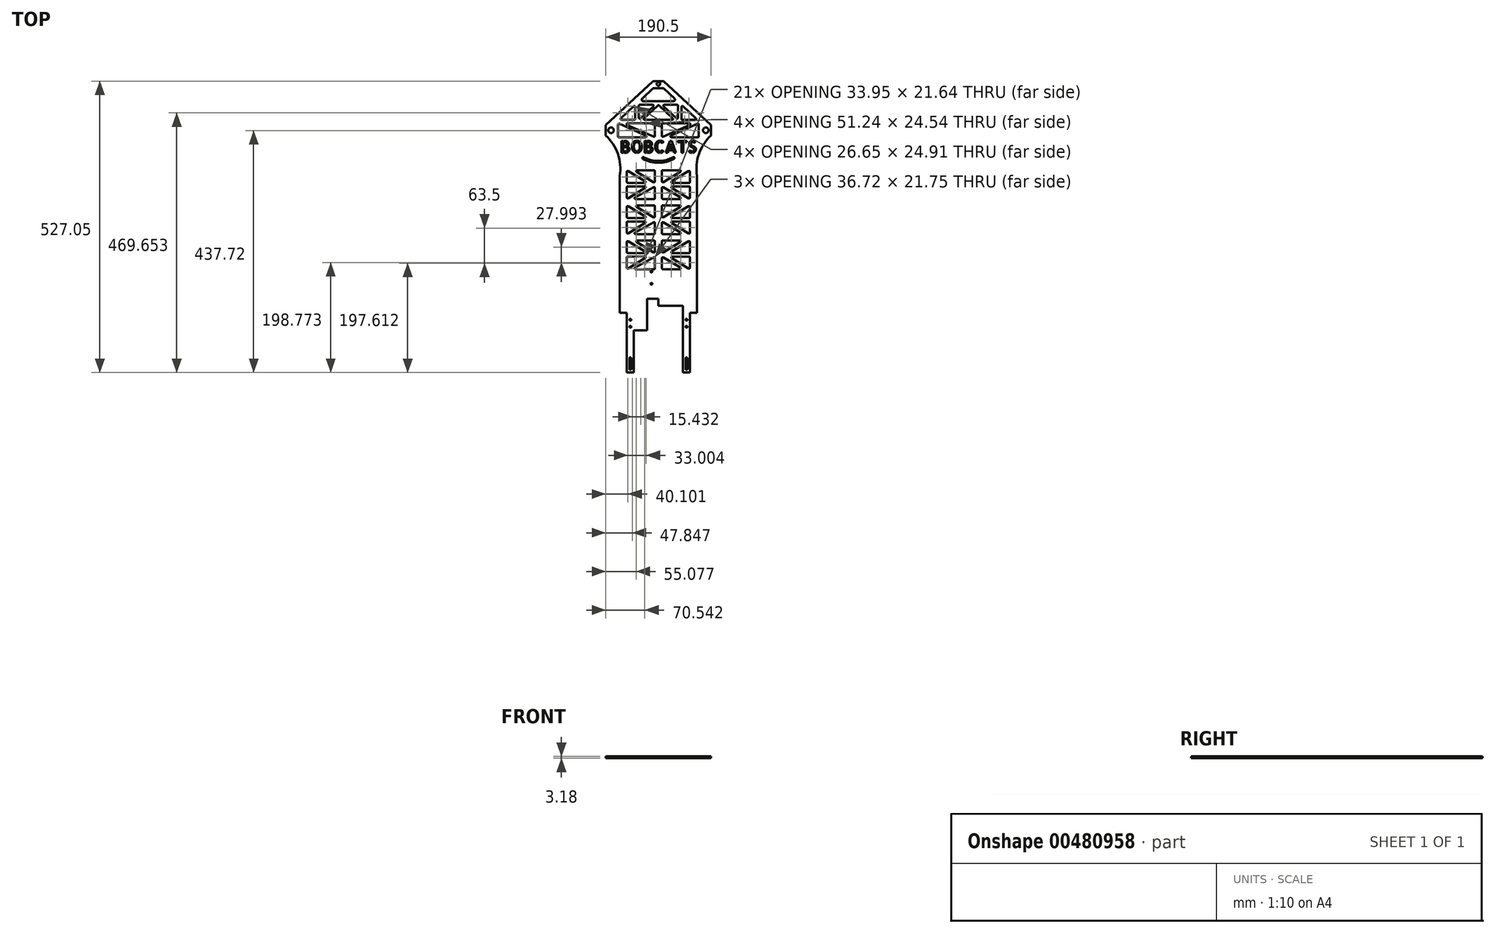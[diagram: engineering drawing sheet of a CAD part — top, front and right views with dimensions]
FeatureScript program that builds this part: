
annotation { "Feature Type Name" : "Feature", "Feature Type Description" : "" }
export const myFeature = defineFeature(function(context is Context, id is Id, definition is map)
    precondition{}
    {
        {
            var Q0;
            Q0=qCreatedBy(makeId("Top.planeOp"),FACE);
            var sketch = newSketch(context, id + "F0", { "sketchPlane" : qUnion([Q0])});
            skLineSegment(sketch, "E0.bottom", {"start": v(0, 0) * mm, "end": v(139.7, 0) * mm});
            skLineSegment(sketch, "E0.left", {"start": v(0, 0) * mm, "end": v(0, 127) * mm});
            skLineSegment(sketch, "E0.right", {"start": v(139.7, 0) * mm, "end": v(139.7, 153) * mm});
            skLineSegment(sketch, "E1.top", {"start": v(12.7, -228.6) * mm, "end": v(25.4, -228.6) * mm});
            skLineSegment(sketch, "E1.left", {"start": v(0, 0) * mm, "end": v(0, -120.65) * mm});
            skLineSegment(sketch, "E1.right", {"start": v(139.7, 0) * mm, "end": v(139.7, -120.65) * mm});
            skPoint(sketch, "E1.middle", {"position": v(69.85, -114.3) * mm});
            skLineSegment(sketch, "E2.top", {"start": v(25.4, -152.4) * mm, "end": v(49.53, -152.4) * mm});
            skLineSegment(sketch, "E2.left", {"start": v(25.4, -228.6) * mm, "end": v(25.4, -152.4) * mm});
            skLineSegment(sketch, "E2.right", {"start": v(114.3, -228.6) * mm, "end": v(114.3, -152.4) * mm});
            skLineSegment(sketch, "E3.top", {"start": v(114.3, -107.95) * mm, "end": v(69.85, -107.95) * mm});
            skLineSegment(sketch, "E3.left", {"start": v(114.3, -152.4) * mm, "end": v(114.3, -107.95) * mm});
            skLineSegment(sketch, "E4.top", {"start": v(69.85, -95.25) * mm, "end": v(49.53, -95.25) * mm});
            skLineSegment(sketch, "E4.left", {"start": v(69.85, -107.95) * mm, "end": v(69.85, -95.25) * mm});
            skLineSegment(sketch, "E4.right", {"start": v(49.53, -152.4) * mm, "end": v(49.53, -95.25) * mm});
            skLineSegment(sketch, "E5.left", {"start": v(25.4, -228.6) * mm, "end": v(25.4, -222.25) * mm});
            skLineSegment(sketch, "E5.right", {"start": v(114.3, -107.11) * mm, "end": v(114.3, -100.76) * mm});
            skPoint(sketch, "E6", {"position": v(57.15, -46.04) * mm});
            skPoint(sketch, "E7", {"position": v(57.15, -68.26) * mm});
            skCircle(sketch, "E8", {"center": v(57.15, -68.26) * mm, "radius": 1.59 * mm});
            skCircle(sketch, "E9", {"center": v(57.15, -46.04) * mm, "radius": 1.59 * mm});
            skLineSegment(sketch, "E10.top", {"start": v(0, -120.65) * mm, "end": v(12.7, -120.65) * mm});
            skLineSegment(sketch, "E10.right", {"start": v(12.7, -228.6) * mm, "end": v(12.7, -120.65) * mm});
            skPoint(sketch, "E11.oppositeSnap0", {"position": v(59.7, -152.4) * mm});
            skLineSegment(sketch, "E12.top", {"start": v(127, -120.65) * mm, "end": v(139.7, -120.65) * mm});
            skLineSegment(sketch, "E12.left", {"start": v(127, -228.6) * mm, "end": v(127, -120.65) * mm});
            skPoint(sketch, "E13.orphan", {"position": v(0, -228.6) * mm});
            skPoint(sketch, "E14.orphan", {"position": v(139.7, -228.6) * mm});
            skLineSegment(sketch, "E15.trimOffspring", {"start": v(114.3, -228.6) * mm, "end": v(127, -228.6) * mm});
            skPoint(sketch, "E3.bottom.end.orphan", {"position": v(69.85, -152.4) * mm});
            skLineSegment(sketch, "E16.bottom", {"start": v(60.32, 298.45) * mm, "end": v(79.38, 298.45) * mm});
            skLineSegment(sketch, "E16.top", {"start": v(0, 127) * mm, "end": v(139.7, 127) * mm});
            skLineSegment(sketch, "E16.left", {"start": v(-25.4, 219.08) * mm, "end": v(-25.4, 200.02) * mm});
            skLineSegment(sketch, "E16.right", {"start": v(165.1, 219.08) * mm, "end": v(165.1, 200.02) * mm});
            skLineSegment(sketch, "E17", {"start": v(60.32, 298.45) * mm, "end": v(-25.4, 219.08) * mm});
            skLineSegment(sketch, "E18", {"start": v(79.38, 298.45) * mm, "end": v(165.1, 219.08) * mm});
            skPoint(sketch, "E19", {"position": v(69.85, 293.37) * mm});
            skPoint(sketch, "E19.positionSnap0", {"position": v(69.85, 298.45) * mm});
            skCircle(sketch, "E20", {"center": v(69.85, 293.37) * mm, "radius": 3.2 * mm});
            skLineSegment(sketch, "E21.bottom", {"start": v(64.34, 298.45) * mm, "end": v(74.5, 298.45) * mm});
            skPoint(sketch, "E22", {"position": v(69.85, 127) * mm});
            skPoint(sketch, "E23", {"position": v(-25.4, 209.55) * mm});
            skPoint(sketch, "E24", {"position": v(165.1, 209.55) * mm});
            skText(sketch, "E25", { "text": "BOBCATS", "fontName": "AllertaStencil-Regular.ttf"});
            skArc(sketch, "E26", {"start": v(0, 127) * mm, "mid": v(-3.47, 166.72) * mm, "end": v(-25.4, 200.03) * mm});
            skLineSegment(sketch, "E27", {"start": v(42.39, 159.43) * mm, "end": v(100.33, 159.43) * mm, "construction": true});
            skArc(sketch, "E28", {"start": v(42.39, 159.43) * mm, "mid": v(69.85, 152.4) * mm, "end": v(97.31, 159.43) * mm, "construction": true});
            skArc(sketch, "E29.0", {"start": v(43.16, 160.83) * mm, "mid": v(69.85, 154) * mm, "end": v(96.54, 160.83) * mm});
            skArc(sketch, "E30.0", {"start": v(41.62, 158.03) * mm, "mid": v(69.85, 150.8) * mm, "end": v(98.08, 158.03) * mm});
            skCircle(sketch, "E31", {"center": v(42.39, 159.43) * mm, "radius": 1.6 * mm});
            skCircle(sketch, "E32", {"center": v(97.31, 159.43) * mm, "radius": 1.6 * mm});
            skLineSegment(sketch, "E33", {"start": v(59.72, 284.9) * mm, "end": v(40.83, 267.42) * mm});
            skLineSegment(sketch, "E34", {"start": v(42.99, 261.91) * mm, "end": v(96.71, 261.91) * mm});
            skLineSegment(sketch, "E35", {"start": v(98.87, 267.42) * mm, "end": v(79.98, 284.9) * mm});
            skLineSegment(sketch, "E36", {"start": v(77.83, 285.75) * mm, "end": v(61.87, 285.75) * mm});
            skPoint(sketch, "E37.visualSharp", {"position": v(60.63, 285.75) * mm});
            skArc(sketch, "E37.filletArc", {"start": v(61.87, 285.75) * mm, "mid": v(60.71, 285.53) * mm, "end": v(59.72, 284.9) * mm});
            skPoint(sketch, "E38.visualSharp", {"position": v(79.07, 285.75) * mm});
            skArc(sketch, "E38.filletArc", {"start": v(79.98, 284.9) * mm, "mid": v(78.99, 285.53) * mm, "end": v(77.83, 285.75) * mm});
            skPoint(sketch, "E39.visualSharp", {"position": v(34.89, 261.91) * mm});
            skArc(sketch, "E39.filletArc", {"start": v(40.83, 267.42) * mm, "mid": v(40.03, 263.93) * mm, "end": v(42.99, 261.91) * mm});
            skPoint(sketch, "E40.visualSharp", {"position": v(104.81, 261.91) * mm});
            skArc(sketch, "E40.filletArc", {"start": v(96.71, 261.91) * mm, "mid": v(99.67, 263.93) * mm, "end": v(98.87, 267.42) * mm});
            skCircle(sketch, "E41", {"center": v(-15.88, 209.55) * mm, "radius": 5 * mm});
            skCircle(sketch, "E42", {"center": v(155.58, 209.55) * mm, "radius": 5 * mm});
            skLineSegment(sketch, "E43", {"start": v(-3.18, 198.44) * mm, "end": v(-3.18, 219.8) * mm});
            skLineSegment(sketch, "E44", {"start": v(-0.94, 221.26) * mm, "end": v(47.14, 199.89) * mm});
            skLineSegment(sketch, "E45", {"start": v(46.5, 196.85) * mm, "end": v(-1.59, 196.85) * mm});
            skLineSegment(sketch, "E46", {"start": v(13.19, 219.21) * mm, "end": v(61.27, 197.84) * mm});
            skLineSegment(sketch, "E47", {"start": v(63.5, 199.3) * mm, "end": v(63.5, 220.66) * mm});
            skLineSegment(sketch, "E48", {"start": v(61.91, 222.25) * mm, "end": v(13.83, 222.25) * mm});
            skLineSegment(sketch, "E49", {"start": v(142.88, 198.44) * mm, "end": v(142.88, 219.8) * mm});
            skLineSegment(sketch, "E50", {"start": v(140.64, 221.26) * mm, "end": v(92.56, 199.89) * mm});
            skLineSegment(sketch, "E51", {"start": v(93.2, 196.85) * mm, "end": v(141.29, 196.85) * mm});
            skLineSegment(sketch, "E52", {"start": v(76.2, 199.3) * mm, "end": v(76.2, 220.66) * mm});
            skLineSegment(sketch, "E53", {"start": v(78.43, 197.84) * mm, "end": v(126.51, 219.21) * mm});
            skLineSegment(sketch, "E54", {"start": v(125.87, 222.25) * mm, "end": v(77.79, 222.25) * mm});
            skPoint(sketch, "E55.visualSharp", {"position": v(6.35, 222.25) * mm});
            skArc(sketch, "E55.filletArc", {"start": v(13.83, 222.25) * mm, "mid": v(12.28, 221) * mm, "end": v(13.19, 219.21) * mm});
            skPoint(sketch, "E56.visualSharp", {"position": v(53.98, 196.85) * mm});
            skArc(sketch, "E56.filletArc", {"start": v(46.5, 196.85) * mm, "mid": v(48.05, 198.1) * mm, "end": v(47.14, 199.89) * mm});
            skPoint(sketch, "E57.visualSharp", {"position": v(-3.18, 222.25) * mm});
            skArc(sketch, "E57.filletArc", {"start": v(-0.94, 221.26) * mm, "mid": v(-2.45, 221.14) * mm, "end": v(-3.18, 219.8) * mm});
            skPoint(sketch, "E58.visualSharp", {"position": v(-3.18, 196.85) * mm});
            skArc(sketch, "E58.filletArc", {"start": v(-3.18, 198.44) * mm, "mid": v(-2.71, 197.31) * mm, "end": v(-1.59, 196.85) * mm});
            skPoint(sketch, "E59.visualSharp", {"position": v(76.2, 222.25) * mm});
            skArc(sketch, "E59.filletArc", {"start": v(77.79, 222.25) * mm, "mid": v(76.66, 221.79) * mm, "end": v(76.2, 220.66) * mm});
            skPoint(sketch, "E60.visualSharp", {"position": v(63.5, 222.25) * mm});
            skArc(sketch, "E60.filletArc", {"start": v(63.5, 220.66) * mm, "mid": v(63.04, 221.79) * mm, "end": v(61.91, 222.25) * mm});
            skPoint(sketch, "E61.visualSharp", {"position": v(63.5, 196.85) * mm});
            skArc(sketch, "E61.filletArc", {"start": v(61.27, 197.84) * mm, "mid": v(62.78, 197.96) * mm, "end": v(63.5, 199.3) * mm});
            skPoint(sketch, "E62.visualSharp", {"position": v(76.2, 196.85) * mm});
            skArc(sketch, "E62.filletArc", {"start": v(76.2, 199.3) * mm, "mid": v(76.92, 197.96) * mm, "end": v(78.43, 197.84) * mm});
            skPoint(sketch, "E63.visualSharp", {"position": v(133.35, 222.25) * mm});
            skArc(sketch, "E63.filletArc", {"start": v(126.51, 219.21) * mm, "mid": v(127.42, 221) * mm, "end": v(125.87, 222.25) * mm});
            skPoint(sketch, "E64.visualSharp", {"position": v(85.72, 196.85) * mm});
            skArc(sketch, "E64.filletArc", {"start": v(92.56, 199.89) * mm, "mid": v(91.65, 198.1) * mm, "end": v(93.2, 196.85) * mm});
            skPoint(sketch, "E65.visualSharp", {"position": v(142.88, 222.25) * mm});
            skArc(sketch, "E65.filletArc", {"start": v(142.88, 219.8) * mm, "mid": v(142.15, 221.14) * mm, "end": v(140.64, 221.26) * mm});
            skPoint(sketch, "E66.visualSharp", {"position": v(142.88, 196.85) * mm});
            skArc(sketch, "E66.filletArc", {"start": v(141.29, 196.85) * mm, "mid": v(142.41, 197.31) * mm, "end": v(142.88, 198.44) * mm});
            skLineSegment(sketch, "E67", {"start": v(68.77, 254.57) * mm, "end": v(43.7, 231.35) * mm});
            skLineSegment(sketch, "E68", {"start": v(44.78, 228.6) * mm, "end": v(94.92, 228.6) * mm});
            skLineSegment(sketch, "E69", {"start": v(96, 231.35) * mm, "end": v(70.93, 254.57) * mm});
            skLineSegment(sketch, "E70", {"start": v(60.53, 252.81) * mm, "end": v(37.04, 231.07) * mm});
            skLineSegment(sketch, "E71", {"start": v(34.38, 232.23) * mm, "end": v(34.38, 253.98) * mm});
            skLineSegment(sketch, "E72", {"start": v(35.97, 255.56) * mm, "end": v(59.45, 255.56) * mm});
            skLineSegment(sketch, "E73", {"start": v(25.36, 253.1) * mm, "end": v(1.88, 231.35) * mm});
            skLineSegment(sketch, "E74", {"start": v(2.96, 228.6) * mm, "end": v(26.44, 228.6) * mm});
            skLineSegment(sketch, "E75", {"start": v(28.03, 230.19) * mm, "end": v(28.03, 251.93) * mm});
            skPoint(sketch, "E76.visualSharp", {"position": v(28.03, 255.56) * mm});
            skArc(sketch, "E76.filletArc", {"start": v(28.03, 251.93) * mm, "mid": v(27.08, 253.39) * mm, "end": v(25.36, 253.1) * mm});
            skPoint(sketch, "E77.visualSharp", {"position": v(-1.1, 228.6) * mm});
            skArc(sketch, "E77.filletArc", {"start": v(1.88, 231.35) * mm, "mid": v(1.48, 229.6) * mm, "end": v(2.96, 228.6) * mm});
            skPoint(sketch, "E78.visualSharp", {"position": v(28.03, 228.6) * mm});
            skArc(sketch, "E78.filletArc", {"start": v(26.44, 228.6) * mm, "mid": v(27.56, 229.06) * mm, "end": v(28.03, 230.19) * mm});
            skPoint(sketch, "E79.visualSharp", {"position": v(34.38, 228.6) * mm});
            skArc(sketch, "E79.filletArc", {"start": v(34.38, 232.23) * mm, "mid": v(35.33, 230.78) * mm, "end": v(37.04, 231.07) * mm});
            skPoint(sketch, "E80.visualSharp", {"position": v(34.38, 255.56) * mm});
            skArc(sketch, "E80.filletArc", {"start": v(35.97, 255.56) * mm, "mid": v(34.84, 255.1) * mm, "end": v(34.38, 253.98) * mm});
            skPoint(sketch, "E81.visualSharp", {"position": v(63.5, 255.56) * mm});
            skArc(sketch, "E81.filletArc", {"start": v(60.53, 252.81) * mm, "mid": v(60.93, 254.56) * mm, "end": v(59.45, 255.56) * mm});
            skPoint(sketch, "E82.visualSharp", {"position": v(69.85, 255.56) * mm});
            skArc(sketch, "E82.filletArc", {"start": v(70.93, 254.57) * mm, "mid": v(69.85, 254.99) * mm, "end": v(68.77, 254.57) * mm});
            skPoint(sketch, "E83.visualSharp", {"position": v(40.73, 228.6) * mm});
            skArc(sketch, "E83.filletArc", {"start": v(43.7, 231.35) * mm, "mid": v(43.3, 229.6) * mm, "end": v(44.78, 228.6) * mm});
            skPoint(sketch, "E84.visualSharp", {"position": v(98.97, 228.6) * mm});
            skArc(sketch, "E84.filletArc", {"start": v(94.92, 228.6) * mm, "mid": v(96.4, 229.6) * mm, "end": v(96, 231.35) * mm});
            skLineSegment(sketch, "E85", {"start": v(69.85, 260.44) * mm, "end": v(69.85, 219.43) * mm});
            skLineSegment(sketch, "E86.MirrorCS", {"start": v(79.17, 252.81) * mm, "end": v(102.66, 231.07) * mm});
            skLineSegment(sketch, "E87.MirrorCS", {"start": v(103.73, 255.56) * mm, "end": v(80.25, 255.56) * mm});
            skLineSegment(sketch, "E88.MirrorCS", {"start": v(105.32, 232.23) * mm, "end": v(105.32, 253.98) * mm});
            skLineSegment(sketch, "E89.MirrorCS", {"start": v(111.67, 230.19) * mm, "end": v(111.67, 251.93) * mm});
            skLineSegment(sketch, "E90.MirrorCS", {"start": v(114.34, 253.1) * mm, "end": v(137.82, 231.35) * mm});
            skLineSegment(sketch, "E91.MirrorCS", {"start": v(136.74, 228.6) * mm, "end": v(113.26, 228.6) * mm});
            skArc(sketch, "E92.MirrorCS", {"start": v(111.67, 251.93) * mm, "mid": v(112.62, 253.39) * mm, "end": v(114.34, 253.1) * mm});
            skArc(sketch, "E93.MirrorCS", {"start": v(113.26, 228.6) * mm, "mid": v(112.14, 229.06) * mm, "end": v(111.67, 230.19) * mm});
            skArc(sketch, "E94.MirrorCS", {"start": v(105.32, 232.23) * mm, "mid": v(104.37, 230.78) * mm, "end": v(102.66, 231.07) * mm});
            skArc(sketch, "E95.MirrorCS", {"start": v(103.73, 255.56) * mm, "mid": v(104.86, 255.1) * mm, "end": v(105.32, 253.98) * mm});
            skArc(sketch, "E96.MirrorCS", {"start": v(79.17, 252.81) * mm, "mid": v(78.77, 254.56) * mm, "end": v(80.25, 255.56) * mm});
            skArc(sketch, "E97.MirrorCS", {"start": v(137.82, 231.35) * mm, "mid": v(138.22, 229.6) * mm, "end": v(136.74, 228.6) * mm});
            skLineSegment(sketch, "E98", {"start": v(12.7, 115.93) * mm, "end": v(12.7, 134.4) * mm});
            skLineSegment(sketch, "E99", {"start": v(15.1, 135.76) * mm, "end": v(45.89, 117.3) * mm});
            skLineSegment(sketch, "E100", {"start": v(45.07, 114.35) * mm, "end": v(14.29, 114.35) * mm});
            skLineSegment(sketch, "E101", {"start": v(30.31, 134.26) * mm, "end": v(61.1, 115.79) * mm});
            skLineSegment(sketch, "E102", {"start": v(63.5, 117.15) * mm, "end": v(63.5, 135.62) * mm});
            skLineSegment(sketch, "E103", {"start": v(61.91, 137.2) * mm, "end": v(31.13, 137.2) * mm});
            skLineSegment(sketch, "E104", {"start": v(76.2, 135.62) * mm, "end": v(76.2, 117.15) * mm});
            skLineSegment(sketch, "E105", {"start": v(78.6, 115.79) * mm, "end": v(109.39, 134.26) * mm});
            skLineSegment(sketch, "E106", {"start": v(108.57, 137.2) * mm, "end": v(77.79, 137.2) * mm});
            skLineSegment(sketch, "E107", {"start": v(124.6, 135.76) * mm, "end": v(93.81, 117.3) * mm});
            skLineSegment(sketch, "E108", {"start": v(94.63, 114.35) * mm, "end": v(125.41, 114.35) * mm});
            skLineSegment(sketch, "E109", {"start": v(127, 115.93) * mm, "end": v(127, 134.4) * mm});
            skArc(sketch, "E110.MirrorCS", {"start": v(139.7, 127) * mm, "mid": v(143.17, 166.72) * mm, "end": v(165.1, 200.03) * mm});
            skLineSegment(sketch, "E111", {"start": v(14.29, 108) * mm, "end": v(45.07, 108) * mm});
            skLineSegment(sketch, "E112", {"start": v(45.89, 105.05) * mm, "end": v(15.1, 86.58) * mm});
            skLineSegment(sketch, "E113", {"start": v(12.7, 87.94) * mm, "end": v(12.7, 106.4) * mm});
            skLineSegment(sketch, "E114", {"start": v(63.5, 105.3) * mm, "end": v(63.5, 86.72) * mm});
            skLineSegment(sketch, "E115", {"start": v(61.91, 85.14) * mm, "end": v(28.37, 85.14) * mm});
            skLineSegment(sketch, "E116", {"start": v(27.6, 88.11) * mm, "end": v(61.14, 106.69) * mm});
            skLineSegment(sketch, "E117", {"start": v(76.2, 105.2) * mm, "end": v(76.2, 86.72) * mm});
            skLineSegment(sketch, "E118", {"start": v(77.79, 85.14) * mm, "end": v(108.57, 85.14) * mm});
            skLineSegment(sketch, "E119", {"start": v(109.39, 88.08) * mm, "end": v(78.6, 106.55) * mm});
            skLineSegment(sketch, "E120", {"start": v(93.81, 105.05) * mm, "end": v(124.6, 86.58) * mm});
            skLineSegment(sketch, "E121", {"start": v(127, 87.94) * mm, "end": v(127, 106.4) * mm});
            skLineSegment(sketch, "E122", {"start": v(125.41, 108) * mm, "end": v(94.63, 108) * mm});
            skPoint(sketch, "E123.visualSharp", {"position": v(12.7, 114.35) * mm});
            skArc(sketch, "E123.filletArc", {"start": v(12.7, 115.93) * mm, "mid": v(13.16, 114.81) * mm, "end": v(14.29, 114.35) * mm});
            skPoint(sketch, "E124.visualSharp", {"position": v(50.8, 114.35) * mm});
            skArc(sketch, "E124.filletArc", {"start": v(45.07, 114.35) * mm, "mid": v(46.6, 115.5) * mm, "end": v(45.89, 117.3) * mm});
            skPoint(sketch, "E125.visualSharp", {"position": v(12.7, 137.2) * mm});
            skArc(sketch, "E125.filletArc", {"start": v(15.1, 135.76) * mm, "mid": v(13.5, 135.78) * mm, "end": v(12.7, 134.4) * mm});
            skPoint(sketch, "E126.visualSharp", {"position": v(25.4, 137.2) * mm});
            skArc(sketch, "E126.filletArc", {"start": v(31.13, 137.2) * mm, "mid": v(29.6, 136.04) * mm, "end": v(30.31, 134.26) * mm});
            skPoint(sketch, "E127.visualSharp", {"position": v(63.5, 137.2) * mm});
            skArc(sketch, "E127.filletArc", {"start": v(63.5, 135.62) * mm, "mid": v(63.04, 136.74) * mm, "end": v(61.91, 137.2) * mm});
            skPoint(sketch, "E128.visualSharp", {"position": v(63.5, 114.35) * mm});
            skArc(sketch, "E128.filletArc", {"start": v(61.1, 115.79) * mm, "mid": v(62.7, 115.77) * mm, "end": v(63.5, 117.15) * mm});
            skPoint(sketch, "E129.visualSharp", {"position": v(76.2, 114.35) * mm});
            skArc(sketch, "E129.filletArc", {"start": v(76.2, 117.15) * mm, "mid": v(77, 115.77) * mm, "end": v(78.6, 115.79) * mm});
            skPoint(sketch, "E130.visualSharp", {"position": v(114.3, 137.2) * mm});
            skArc(sketch, "E130.filletArc", {"start": v(109.39, 134.26) * mm, "mid": v(110.1, 136.04) * mm, "end": v(108.57, 137.2) * mm});
            skPoint(sketch, "E131.visualSharp", {"position": v(76.2, 137.2) * mm});
            skArc(sketch, "E131.filletArc", {"start": v(77.79, 137.2) * mm, "mid": v(76.66, 136.74) * mm, "end": v(76.2, 135.62) * mm});
            skPoint(sketch, "E132.visualSharp", {"position": v(127, 137.2) * mm});
            skArc(sketch, "E132.filletArc", {"start": v(127, 134.4) * mm, "mid": v(126.2, 135.78) * mm, "end": v(124.6, 135.76) * mm});
            skPoint(sketch, "E133.visualSharp", {"position": v(88.9, 114.35) * mm});
            skArc(sketch, "E133.filletArc", {"start": v(93.81, 117.3) * mm, "mid": v(93.1, 115.5) * mm, "end": v(94.63, 114.35) * mm});
            skPoint(sketch, "E134.visualSharp", {"position": v(127, 114.35) * mm});
            skArc(sketch, "E134.filletArc", {"start": v(125.41, 114.35) * mm, "mid": v(126.54, 114.81) * mm, "end": v(127, 115.93) * mm});
            skPoint(sketch, "E135.visualSharp", {"position": v(12.7, 108) * mm});
            skArc(sketch, "E135.filletArc", {"start": v(14.29, 108) * mm, "mid": v(13.16, 107.53) * mm, "end": v(12.7, 106.4) * mm});
            skPoint(sketch, "E136.visualSharp", {"position": v(50.8, 108) * mm});
            skArc(sketch, "E136.filletArc", {"start": v(45.89, 105.05) * mm, "mid": v(46.6, 106.83) * mm, "end": v(45.07, 108) * mm});
            skPoint(sketch, "E137.visualSharp", {"position": v(63.5, 108) * mm});
            skArc(sketch, "E137.filletArc", {"start": v(63.5, 105.3) * mm, "mid": v(62.72, 106.67) * mm, "end": v(61.14, 106.69) * mm});
            skPoint(sketch, "E138.visualSharp", {"position": v(63.5, 85.14) * mm});
            skArc(sketch, "E138.filletArc", {"start": v(61.91, 85.14) * mm, "mid": v(63.04, 85.6) * mm, "end": v(63.5, 86.72) * mm});
            skPoint(sketch, "E139.visualSharp", {"position": v(22.23, 85.14) * mm});
            skArc(sketch, "E139.filletArc", {"start": v(27.6, 88.11) * mm, "mid": v(26.83, 86.33) * mm, "end": v(28.37, 85.14) * mm});
            skPoint(sketch, "E140.visualSharp", {"position": v(76.2, 85.14) * mm});
            skArc(sketch, "E140.filletArc", {"start": v(76.2, 86.72) * mm, "mid": v(76.66, 85.6) * mm, "end": v(77.79, 85.14) * mm});
            skPoint(sketch, "E141.visualSharp", {"position": v(114.3, 85.14) * mm});
            skArc(sketch, "E141.filletArc", {"start": v(108.57, 85.14) * mm, "mid": v(110.1, 86.3) * mm, "end": v(109.39, 88.08) * mm});
            skPoint(sketch, "E142.visualSharp", {"position": v(76.2, 108) * mm});
            skArc(sketch, "E142.filletArc", {"start": v(78.6, 106.55) * mm, "mid": v(77, 106.57) * mm, "end": v(76.2, 105.2) * mm});
            skPoint(sketch, "E143.visualSharp", {"position": v(88.9, 108) * mm});
            skArc(sketch, "E143.filletArc", {"start": v(94.63, 108) * mm, "mid": v(93.1, 106.83) * mm, "end": v(93.81, 105.05) * mm});
            skPoint(sketch, "E144.visualSharp", {"position": v(127, 108) * mm});
            skArc(sketch, "E144.filletArc", {"start": v(127, 106.4) * mm, "mid": v(126.54, 107.53) * mm, "end": v(125.41, 108) * mm});
            skPoint(sketch, "E145.visualSharp", {"position": v(127, 85.14) * mm});
            skArc(sketch, "E145.filletArc", {"start": v(124.6, 86.58) * mm, "mid": v(126.2, 86.56) * mm, "end": v(127, 87.94) * mm});
            skPoint(sketch, "E146.visualSharp", {"position": v(12.7, 85.14) * mm});
            skArc(sketch, "E146.filletArc", {"start": v(12.7, 87.94) * mm, "mid": v(13.5, 86.56) * mm, "end": v(15.1, 86.58) * mm});
            skLineSegment(sketch, "E147.0.1.0", {"start": v(127, 24.44) * mm, "end": v(127, 42.9) * mm});
            skArc(sketch, "E147.0.1.1", {"start": v(108.57, 21.64) * mm, "mid": v(110.1, 22.8) * mm, "end": v(109.39, 24.58) * mm});
            skPoint(sketch, "E147.0.1.2", {"position": v(88.9, 44.5) * mm});
            skLineSegment(sketch, "E147.0.1.3", {"start": v(127, 52.43) * mm, "end": v(127, 70.9) * mm});
            skLineSegment(sketch, "E147.0.1.4", {"start": v(45.07, 50.85) * mm, "end": v(14.29, 50.85) * mm});
            skLineSegment(sketch, "E147.0.1.5", {"start": v(61.91, 73.7) * mm, "end": v(31.13, 73.7) * mm});
            skArc(sketch, "E147.0.1.6", {"start": v(94.63, 44.5) * mm, "mid": v(93.1, 43.33) * mm, "end": v(93.81, 41.55) * mm});
            skLineSegment(sketch, "E147.0.1.7", {"start": v(77.79, 21.64) * mm, "end": v(108.57, 21.64) * mm});
            skPoint(sketch, "E147.0.1.8", {"position": v(127, 44.5) * mm});
            skPoint(sketch, "E147.0.1.9", {"position": v(76.2, 73.7) * mm});
            skPoint(sketch, "E147.0.1.10", {"position": v(127, 21.64) * mm});
            skPoint(sketch, "E147.0.1.11", {"position": v(63.5, 44.5) * mm});
            skArc(sketch, "E147.0.1.12", {"start": v(45.07, 50.85) * mm, "mid": v(46.6, 52) * mm, "end": v(45.89, 53.8) * mm});
            skLineSegment(sketch, "E147.0.1.13", {"start": v(124.6, 72.26) * mm, "end": v(93.81, 53.8) * mm});
            skPoint(sketch, "E147.0.1.14", {"position": v(22.23, 21.64) * mm});
            skPoint(sketch, "E147.0.1.15", {"position": v(63.5, 50.85) * mm});
            skArc(sketch, "E147.0.1.16", {"start": v(61.1, 52.29) * mm, "mid": v(62.7, 52.27) * mm, "end": v(63.5, 53.65) * mm});
            skPoint(sketch, "E147.0.1.17", {"position": v(25.4, 73.7) * mm});
            skPoint(sketch, "E147.0.1.18", {"position": v(63.5, 21.64) * mm});
            skLineSegment(sketch, "E147.0.1.19", {"start": v(61.91, 21.64) * mm, "end": v(28.37, 21.64) * mm});
            skLineSegment(sketch, "E147.0.1.20", {"start": v(30.31, 70.76) * mm, "end": v(61.1, 52.29) * mm});
            skLineSegment(sketch, "E147.0.1.21", {"start": v(63.5, 41.8) * mm, "end": v(63.5, 23.22) * mm});
            skPoint(sketch, "E147.0.1.22", {"position": v(76.2, 50.85) * mm});
            skLineSegment(sketch, "E147.0.1.23", {"start": v(125.41, 44.5) * mm, "end": v(94.63, 44.5) * mm});
            skPoint(sketch, "E147.0.1.24", {"position": v(12.7, 44.5) * mm});
            skArc(sketch, "E147.0.1.25", {"start": v(12.7, 24.44) * mm, "mid": v(13.5, 23.06) * mm, "end": v(15.1, 23.08) * mm});
            skPoint(sketch, "E147.0.1.26", {"position": v(69.85, 63.5) * mm});
            skLineSegment(sketch, "E147.0.1.27", {"start": v(27.6, 24.61) * mm, "end": v(61.14, 43.19) * mm});
            skLineSegment(sketch, "E147.0.1.28", {"start": v(63.5, 53.65) * mm, "end": v(63.5, 72.12) * mm});
            skPoint(sketch, "E147.0.1.29", {"position": v(12.7, 21.64) * mm});
            skPoint(sketch, "E147.0.1.30", {"position": v(76.2, 44.5) * mm});
            skArc(sketch, "E147.0.1.31", {"start": v(15.1, 72.26) * mm, "mid": v(13.5, 72.28) * mm, "end": v(12.7, 70.9) * mm});
            skPoint(sketch, "E147.0.1.32", {"position": v(127, 73.7) * mm});
            skArc(sketch, "E147.0.1.33", {"start": v(63.5, 41.8) * mm, "mid": v(62.72, 43.17) * mm, "end": v(61.14, 43.19) * mm});
            skLineSegment(sketch, "E147.0.1.34", {"start": v(14.29, 44.5) * mm, "end": v(45.07, 44.5) * mm});
            skLineSegment(sketch, "E147.0.1.35", {"start": v(108.57, 73.7) * mm, "end": v(77.79, 73.7) * mm});
            skPoint(sketch, "E147.0.1.36", {"position": v(114.3, 21.64) * mm});
            skLineSegment(sketch, "E147.0.1.37", {"start": v(45.89, 41.55) * mm, "end": v(15.1, 23.08) * mm});
            skPoint(sketch, "E147.0.1.38", {"position": v(63.5, 73.7) * mm});
            skPoint(sketch, "E147.0.1.39", {"position": v(76.2, 21.64) * mm});
            skArc(sketch, "E147.0.1.40", {"start": v(124.6, 23.08) * mm, "mid": v(126.2, 23.06) * mm, "end": v(127, 24.44) * mm});
            skPoint(sketch, "E147.0.1.41", {"position": v(12.7, 73.7) * mm});
            skPoint(sketch, "E147.0.1.42", {"position": v(50.8, 50.85) * mm});
            skLineSegment(sketch, "E147.0.1.43", {"start": v(94.63, 50.85) * mm, "end": v(125.41, 50.85) * mm});
            skPoint(sketch, "E147.0.1.44", {"position": v(88.9, 50.85) * mm});
            skLineSegment(sketch, "E147.0.1.45", {"start": v(12.7, 52.43) * mm, "end": v(12.7, 70.9) * mm});
            skPoint(sketch, "E147.0.1.46", {"position": v(114.3, 73.7) * mm});
            skPoint(sketch, "E147.0.1.47", {"position": v(50.8, 44.5) * mm});
            skLineSegment(sketch, "E147.0.1.48", {"start": v(109.39, 24.58) * mm, "end": v(78.6, 43.05) * mm});
            skArc(sketch, "E147.0.1.49", {"start": v(78.6, 43.05) * mm, "mid": v(77, 43.07) * mm, "end": v(76.2, 41.7) * mm});
            skPoint(sketch, "E147.0.1.50", {"position": v(127, 50.85) * mm});
            skArc(sketch, "E147.0.1.51", {"start": v(127, 70.9) * mm, "mid": v(126.2, 72.28) * mm, "end": v(124.6, 72.26) * mm});
            skLineSegment(sketch, "E147.0.1.52", {"start": v(93.81, 41.55) * mm, "end": v(124.6, 23.08) * mm});
            skLineSegment(sketch, "E147.0.1.53", {"start": v(78.6, 52.29) * mm, "end": v(109.39, 70.76) * mm});
            skArc(sketch, "E147.0.1.54", {"start": v(45.89, 41.55) * mm, "mid": v(46.6, 43.33) * mm, "end": v(45.07, 44.5) * mm});
            skLineSegment(sketch, "E147.0.1.55", {"start": v(15.1, 72.26) * mm, "end": v(45.89, 53.8) * mm});
            skArc(sketch, "E147.0.1.56", {"start": v(27.6, 24.61) * mm, "mid": v(26.83, 22.83) * mm, "end": v(28.37, 21.64) * mm});
            skArc(sketch, "E147.0.1.57", {"start": v(93.81, 53.8) * mm, "mid": v(93.1, 52) * mm, "end": v(94.63, 50.85) * mm});
            skPoint(sketch, "E147.0.1.58", {"position": v(12.7, 50.85) * mm});
            skLineSegment(sketch, "E147.0.1.59", {"start": v(76.2, 72.12) * mm, "end": v(76.2, 53.65) * mm});
            skLineSegment(sketch, "E147.0.1.60", {"start": v(76.2, 41.7) * mm, "end": v(76.2, 23.22) * mm});
            skLineSegment(sketch, "E147.0.1.61", {"start": v(12.7, 24.44) * mm, "end": v(12.7, 42.9) * mm});
            skArc(sketch, "E147.0.1.62", {"start": v(76.2, 53.65) * mm, "mid": v(77, 52.27) * mm, "end": v(78.6, 52.29) * mm});
            skArc(sketch, "E147.0.1.63", {"start": v(12.7, 52.43) * mm, "mid": v(13.16, 51.31) * mm, "end": v(14.29, 50.85) * mm});
            skArc(sketch, "E147.0.1.64", {"start": v(14.29, 44.5) * mm, "mid": v(13.16, 44.03) * mm, "end": v(12.7, 42.9) * mm});
            skArc(sketch, "E147.0.1.65", {"start": v(127, 42.9) * mm, "mid": v(126.54, 44.03) * mm, "end": v(125.41, 44.5) * mm});
            skArc(sketch, "E147.0.1.66", {"start": v(109.39, 70.76) * mm, "mid": v(110.1, 72.54) * mm, "end": v(108.57, 73.7) * mm});
            skArc(sketch, "E147.0.1.67", {"start": v(61.91, 21.64) * mm, "mid": v(63.04, 22.1) * mm, "end": v(63.5, 23.22) * mm});
            skArc(sketch, "E147.0.1.68", {"start": v(31.13, 73.7) * mm, "mid": v(29.6, 72.54) * mm, "end": v(30.31, 70.76) * mm});
            skArc(sketch, "E147.0.1.69", {"start": v(63.5, 72.12) * mm, "mid": v(63.04, 73.24) * mm, "end": v(61.91, 73.7) * mm});
            skArc(sketch, "E147.0.1.70", {"start": v(77.79, 73.7) * mm, "mid": v(76.66, 73.24) * mm, "end": v(76.2, 72.12) * mm});
            skArc(sketch, "E147.0.1.71", {"start": v(76.2, 23.22) * mm, "mid": v(76.66, 22.1) * mm, "end": v(77.79, 21.64) * mm});
            skArc(sketch, "E147.0.1.72", {"start": v(125.41, 50.85) * mm, "mid": v(126.54, 51.31) * mm, "end": v(127, 52.43) * mm});
            skLineSegment(sketch, "E147.0.2.0", {"start": v(127, -39.06) * mm, "end": v(127, -20.6) * mm});
            skArc(sketch, "E147.0.2.1", {"start": v(108.57, -41.86) * mm, "mid": v(110.1, -40.7) * mm, "end": v(109.39, -38.92) * mm});
            skPoint(sketch, "E147.0.2.2", {"position": v(88.9, -19) * mm});
            skLineSegment(sketch, "E147.0.2.3", {"start": v(127, -11.07) * mm, "end": v(127, 7.4) * mm});
            skLineSegment(sketch, "E147.0.2.4", {"start": v(45.07, -12.65) * mm, "end": v(14.29, -12.65) * mm});
            skLineSegment(sketch, "E147.0.2.5", {"start": v(61.91, 10.2) * mm, "end": v(31.13, 10.2) * mm});
            skArc(sketch, "E147.0.2.6", {"start": v(94.63, -19) * mm, "mid": v(93.1, -20.17) * mm, "end": v(93.81, -21.95) * mm});
            skLineSegment(sketch, "E147.0.2.7", {"start": v(77.79, -41.86) * mm, "end": v(108.57, -41.86) * mm});
            skPoint(sketch, "E147.0.2.8", {"position": v(127, -19) * mm});
            skPoint(sketch, "E147.0.2.9", {"position": v(76.2, 10.2) * mm});
            skPoint(sketch, "E147.0.2.10", {"position": v(127, -41.86) * mm});
            skPoint(sketch, "E147.0.2.11", {"position": v(63.5, -19) * mm});
            skArc(sketch, "E147.0.2.12", {"start": v(45.07, -12.65) * mm, "mid": v(46.6, -11.5) * mm, "end": v(45.89, -9.7) * mm});
            skLineSegment(sketch, "E147.0.2.13", {"start": v(124.6, 8.76) * mm, "end": v(93.81, -9.7) * mm});
            skPoint(sketch, "E147.0.2.14", {"position": v(22.23, -41.86) * mm});
            skPoint(sketch, "E147.0.2.15", {"position": v(63.5, -12.65) * mm});
            skArc(sketch, "E147.0.2.16", {"start": v(61.1, -11.21) * mm, "mid": v(62.7, -11.23) * mm, "end": v(63.5, -9.85) * mm});
            skPoint(sketch, "E147.0.2.17", {"position": v(25.4, 10.2) * mm});
            skPoint(sketch, "E147.0.2.18", {"position": v(63.5, -41.86) * mm});
            skLineSegment(sketch, "E147.0.2.19", {"start": v(61.91, -41.86) * mm, "end": v(28.37, -41.86) * mm});
            skLineSegment(sketch, "E147.0.2.20", {"start": v(30.31, 7.26) * mm, "end": v(61.1, -11.21) * mm});
            skLineSegment(sketch, "E147.0.2.21", {"start": v(63.5, -21.7) * mm, "end": v(63.5, -40.28) * mm});
            skPoint(sketch, "E147.0.2.22", {"position": v(76.2, -12.65) * mm});
            skLineSegment(sketch, "E147.0.2.23", {"start": v(125.41, -19) * mm, "end": v(94.63, -19) * mm});
            skPoint(sketch, "E147.0.2.24", {"position": v(12.7, -19) * mm});
            skArc(sketch, "E147.0.2.25", {"start": v(12.7, -39.06) * mm, "mid": v(13.5, -40.44) * mm, "end": v(15.1, -40.42) * mm});
            skPoint(sketch, "E147.0.2.26", {"position": v(69.85, 0) * mm});
            skLineSegment(sketch, "E147.0.2.27", {"start": v(27.6, -38.89) * mm, "end": v(61.14, -20.31) * mm});
            skLineSegment(sketch, "E147.0.2.28", {"start": v(63.5, -9.85) * mm, "end": v(63.5, 8.62) * mm});
            skPoint(sketch, "E147.0.2.29", {"position": v(12.7, -41.86) * mm});
            skPoint(sketch, "E147.0.2.30", {"position": v(76.2, -19) * mm});
            skArc(sketch, "E147.0.2.31", {"start": v(15.1, 8.76) * mm, "mid": v(13.5, 8.78) * mm, "end": v(12.7, 7.4) * mm});
            skPoint(sketch, "E147.0.2.32", {"position": v(127, 10.2) * mm});
            skArc(sketch, "E147.0.2.33", {"start": v(63.5, -21.7) * mm, "mid": v(62.72, -20.33) * mm, "end": v(61.14, -20.31) * mm});
            skLineSegment(sketch, "E147.0.2.34", {"start": v(14.29, -19) * mm, "end": v(45.07, -19) * mm});
            skLineSegment(sketch, "E147.0.2.35", {"start": v(108.57, 10.2) * mm, "end": v(77.79, 10.2) * mm});
            skPoint(sketch, "E147.0.2.36", {"position": v(114.3, -41.86) * mm});
            skLineSegment(sketch, "E147.0.2.37", {"start": v(45.89, -21.95) * mm, "end": v(15.1, -40.42) * mm});
            skPoint(sketch, "E147.0.2.38", {"position": v(63.5, 10.2) * mm});
            skPoint(sketch, "E147.0.2.39", {"position": v(76.2, -41.86) * mm});
            skArc(sketch, "E147.0.2.40", {"start": v(124.6, -40.42) * mm, "mid": v(126.2, -40.44) * mm, "end": v(127, -39.06) * mm});
            skPoint(sketch, "E147.0.2.41", {"position": v(12.7, 10.2) * mm});
            skPoint(sketch, "E147.0.2.42", {"position": v(50.8, -12.65) * mm});
            skLineSegment(sketch, "E147.0.2.43", {"start": v(94.63, -12.65) * mm, "end": v(125.41, -12.65) * mm});
            skPoint(sketch, "E147.0.2.44", {"position": v(88.9, -12.65) * mm});
            skLineSegment(sketch, "E147.0.2.45", {"start": v(12.7, -11.07) * mm, "end": v(12.7, 7.4) * mm});
            skPoint(sketch, "E147.0.2.46", {"position": v(114.3, 10.2) * mm});
            skPoint(sketch, "E147.0.2.47", {"position": v(50.8, -19) * mm});
            skLineSegment(sketch, "E147.0.2.48", {"start": v(109.39, -38.92) * mm, "end": v(78.6, -20.45) * mm});
            skArc(sketch, "E147.0.2.49", {"start": v(78.6, -20.45) * mm, "mid": v(77, -20.43) * mm, "end": v(76.2, -21.8) * mm});
            skPoint(sketch, "E147.0.2.50", {"position": v(127, -12.65) * mm});
            skArc(sketch, "E147.0.2.51", {"start": v(127, 7.4) * mm, "mid": v(126.2, 8.78) * mm, "end": v(124.6, 8.76) * mm});
            skLineSegment(sketch, "E147.0.2.52", {"start": v(93.81, -21.95) * mm, "end": v(124.6, -40.42) * mm});
            skLineSegment(sketch, "E147.0.2.53", {"start": v(78.6, -11.21) * mm, "end": v(109.39, 7.26) * mm});
            skArc(sketch, "E147.0.2.54", {"start": v(45.89, -21.95) * mm, "mid": v(46.6, -20.17) * mm, "end": v(45.07, -19) * mm});
            skLineSegment(sketch, "E147.0.2.55", {"start": v(15.1, 8.76) * mm, "end": v(45.89, -9.7) * mm});
            skArc(sketch, "E147.0.2.56", {"start": v(27.6, -38.89) * mm, "mid": v(26.83, -40.67) * mm, "end": v(28.37, -41.86) * mm});
            skArc(sketch, "E147.0.2.57", {"start": v(93.81, -9.7) * mm, "mid": v(93.1, -11.5) * mm, "end": v(94.63, -12.65) * mm});
            skPoint(sketch, "E147.0.2.58", {"position": v(12.7, -12.65) * mm});
            skLineSegment(sketch, "E147.0.2.59", {"start": v(76.2, 8.62) * mm, "end": v(76.2, -9.85) * mm});
            skLineSegment(sketch, "E147.0.2.60", {"start": v(76.2, -21.8) * mm, "end": v(76.2, -40.28) * mm});
            skLineSegment(sketch, "E147.0.2.61", {"start": v(12.7, -39.06) * mm, "end": v(12.7, -20.6) * mm});
            skArc(sketch, "E147.0.2.62", {"start": v(76.2, -9.85) * mm, "mid": v(77, -11.23) * mm, "end": v(78.6, -11.21) * mm});
            skArc(sketch, "E147.0.2.63", {"start": v(12.7, -11.07) * mm, "mid": v(13.16, -12.19) * mm, "end": v(14.29, -12.65) * mm});
            skArc(sketch, "E147.0.2.64", {"start": v(14.29, -19) * mm, "mid": v(13.16, -19.47) * mm, "end": v(12.7, -20.6) * mm});
            skArc(sketch, "E147.0.2.65", {"start": v(127, -20.6) * mm, "mid": v(126.54, -19.47) * mm, "end": v(125.41, -19) * mm});
            skArc(sketch, "E147.0.2.66", {"start": v(109.39, 7.26) * mm, "mid": v(110.1, 9.04) * mm, "end": v(108.57, 10.2) * mm});
            skArc(sketch, "E147.0.2.67", {"start": v(61.91, -41.86) * mm, "mid": v(63.04, -41.4) * mm, "end": v(63.5, -40.28) * mm});
            skArc(sketch, "E147.0.2.68", {"start": v(31.13, 10.2) * mm, "mid": v(29.6, 9.04) * mm, "end": v(30.31, 7.26) * mm});
            skArc(sketch, "E147.0.2.69", {"start": v(63.5, 8.62) * mm, "mid": v(63.04, 9.74) * mm, "end": v(61.91, 10.2) * mm});
            skArc(sketch, "E147.0.2.70", {"start": v(77.79, 10.2) * mm, "mid": v(76.66, 9.74) * mm, "end": v(76.2, 8.62) * mm});
            skArc(sketch, "E147.0.2.71", {"start": v(76.2, -40.28) * mm, "mid": v(76.66, -41.4) * mm, "end": v(77.79, -41.86) * mm});
            skArc(sketch, "E147.0.2.72", {"start": v(125.41, -12.65) * mm, "mid": v(126.54, -12.19) * mm, "end": v(127, -11.07) * mm});
            skLineSegment(sketch, "E147.direction1", {"start": v(12.7, 85.14) * mm, "end": v(38.1, 85.14) * mm, "construction": true});
            skLineSegment(sketch, "E147.direction2", {"start": v(12.7, 85.14) * mm, "end": v(12.7, 21.64) * mm, "construction": true});
            const initialGuessF0  = {"E25": [0, 0.16896, 1, 0, 0.02154]};
            skSetInitialGuess(sketch, initialGuessF0);
            skSolve(sketch);
        }
        {
            var Q0;
            Q0=makeQuery(id+"F0.imprint","IMPRINT",FACE,{"disambiguationData":[TD([[makeQuery(id+"F0.imprint","IMPRINT",EDGE,{"derivedFrom":sQuery(id+"F0.wireOp",EDGE,"E0.left")}),-1.0]])]});
            var Q1;
            Q1=makeQuery(id+"F0.imprint","IMPRINT",FACE,{"disambiguationData":[TD([[makeQuery(id+"F0.imprint","IMPRINT",EDGE,{"derivedFrom":sQuery(id+"F0.wireOp",EDGE,"E0.bottom")}),-1.0]])]});
            var Q2;
            Q2=makeQuery(id+"F0.imprint","IMPRINT",FACE,{"disambiguationData":[TD([[makeQuery(id+"F0.imprint","IMPRINT",EDGE,{"derivedFrom":sQuery(id+"F0.wireOp",EDGE,"E16.top")}),1.0]])]});
            var Q3;
            Q3=makeQuery(id+"F0.imprint","IMPRINT",FACE,{"disambiguationData":[TD([[makeQuery(id+"F0.imprint","IMPRINT",EDGE,{"derivedFrom":sQuery(id+"F0.wireOp",EDGE,"E20")}),-1.0]])]});
            extrude(context, id + "F1", {"entities" : qUnion([Q0, Q1, Q2, Q3]), "depth" : 3.17 * mm});
        }
        {
            var Q0;
            Q0=makeQuery(id+"F1.opExtrude","CAP_FACE",FACE,{"disambiguationData":[OSD([sQuery(id+"F0.wireOp",EDGE,"E0.left"),sQuery(id+"F0.wireOp",EDGE,"E0.right"),sQuery(id+"F0.wireOp",EDGE,"E1.top"),sQuery(id+"F0.wireOp",EDGE,"E1.left"),sQuery(id+"F0.wireOp",EDGE,"E1.right"),sQuery(id+"F0.wireOp",EDGE,"E2.top"),sQuery(id+"F0.wireOp",EDGE,"E2.left"),sQuery(id+"F0.wireOp",EDGE,"E2.right"),sQuery(id+"F0.wireOp",EDGE,"E3.top"),sQuery(id+"F0.wireOp",EDGE,"E3.left"),sQuery(id+"F0.wireOp",EDGE,"E4.top"),sQuery(id+"F0.wireOp",EDGE,"E4.left"),sQuery(id+"F0.wireOp",EDGE,"E4.right"),sQuery(id+"F0.wireOp",EDGE,"E5.left"),sQuery(id+"F0.wireOp",EDGE,"E10.top"),sQuery(id+"F0.wireOp",EDGE,"E10.right"),sQuery(id+"F0.wireOp",EDGE,"E12.top"),sQuery(id+"F0.wireOp",EDGE,"E12.left"),sQuery(id+"F0.wireOp",EDGE,"E9"),sQuery(id+"F0.wireOp",EDGE,"E8"),sQuery(id+"F0.wireOp",EDGE,"E15.trimOffspring"),sQuery(id+"F0.wireOp",EDGE,"E16.bottom"),sQuery(id+"F0.wireOp",EDGE,"E16.left"),sQuery(id+"F0.wireOp",EDGE,"E16.right"),sQuery(id+"F0.wireOp",EDGE,"E17"),sQuery(id+"F0.wireOp",EDGE,"E18"),sQuery(id+"F0.wireOp",EDGE,"E20"),sQuery(id+"F0.wireOp",EDGE,"E21.bottom"),sQuery(id+"F0.wireOp",EDGE,"E25.sketch_text.stroke-0"),sQuery(id+"F0.wireOp",EDGE,"E25.sketch_text.stroke-1"),sQuery(id+"F0.wireOp",EDGE,"E25.sketch_text.stroke-2"),sQuery(id+"F0.wireOp",EDGE,"E25.sketch_text.stroke-3"),sQuery(id+"F0.wireOp",EDGE,"E25.sketch_text.stroke-4"),sQuery(id+"F0.wireOp",EDGE,"E25.sketch_text.stroke-5"),sQuery(id+"F0.wireOp",EDGE,"E25.sketch_text.stroke-6"),sQuery(id+"F0.wireOp",EDGE,"E25.sketch_text.stroke-7"),sQuery(id+"F0.wireOp",EDGE,"E25.sketch_text.stroke-8"),sQuery(id+"F0.wireOp",EDGE,"E25.sketch_text.stroke-9"),sQuery(id+"F0.wireOp",EDGE,"E25.sketch_text.stroke-10"),sQuery(id+"F0.wireOp",EDGE,"E25.sketch_text.stroke-11"),sQuery(id+"F0.wireOp",EDGE,"E25.sketch_text.stroke-12"),sQuery(id+"F0.wireOp",EDGE,"E25.sketch_text.stroke-13"),sQuery(id+"F0.wireOp",EDGE,"E25.sketch_text.stroke-14"),sQuery(id+"F0.wireOp",EDGE,"E25.sketch_text.stroke-15"),sQuery(id+"F0.wireOp",EDGE,"E25.sketch_text.stroke-16"),sQuery(id+"F0.wireOp",EDGE,"E25.sketch_text.stroke-17"),sQuery(id+"F0.wireOp",EDGE,"E25.sketch_text.stroke-18"),sQuery(id+"F0.wireOp",EDGE,"E25.sketch_text.stroke-19"),sQuery(id+"F0.wireOp",EDGE,"E25.sketch_text.stroke-20"),sQuery(id+"F0.wireOp",EDGE,"E25.sketch_text.stroke-21"),sQuery(id+"F0.wireOp",EDGE,"E25.sketch_text.stroke-22"),sQuery(id+"F0.wireOp",EDGE,"E25.sketch_text.stroke-23"),sQuery(id+"F0.wireOp",EDGE,"E25.sketch_text.stroke-24"),sQuery(id+"F0.wireOp",EDGE,"E25.sketch_text.stroke-25"),sQuery(id+"F0.wireOp",EDGE,"E25.sketch_text.stroke-26"),sQuery(id+"F0.wireOp",EDGE,"E25.sketch_text.stroke-27"),sQuery(id+"F0.wireOp",EDGE,"E25.sketch_text.stroke-28"),sQuery(id+"F0.wireOp",EDGE,"E25.sketch_text.stroke-29"),sQuery(id+"F0.wireOp",EDGE,"E25.sketch_text.stroke-30"),sQuery(id+"F0.wireOp",EDGE,"E25.sketch_text.stroke-31"),sQuery(id+"F0.wireOp",EDGE,"E25.sketch_text.stroke-32"),sQuery(id+"F0.wireOp",EDGE,"E25.sketch_text.stroke-33"),sQuery(id+"F0.wireOp",EDGE,"E25.sketch_text.stroke-34"),sQuery(id+"F0.wireOp",EDGE,"E25.sketch_text.stroke-35"),sQuery(id+"F0.wireOp",EDGE,"E25.sketch_text.stroke-36"),sQuery(id+"F0.wireOp",EDGE,"E25.sketch_text.stroke-37"),sQuery(id+"F0.wireOp",EDGE,"E25.sketch_text.stroke-38"),sQuery(id+"F0.wireOp",EDGE,"E25.sketch_text.stroke-39"),sQuery(id+"F0.wireOp",EDGE,"E25.sketch_text.stroke-40"),sQuery(id+"F0.wireOp",EDGE,"E25.sketch_text.stroke-41"),sQuery(id+"F0.wireOp",EDGE,"E25.sketch_text.stroke-42"),sQuery(id+"F0.wireOp",EDGE,"E25.sketch_text.stroke-43"),sQuery(id+"F0.wireOp",EDGE,"E25.sketch_text.stroke-44"),sQuery(id+"F0.wireOp",EDGE,"E25.sketch_text.stroke-45"),sQuery(id+"F0.wireOp",EDGE,"E25.sketch_text.stroke-46"),sQuery(id+"F0.wireOp",EDGE,"E25.sketch_text.stroke-47"),sQuery(id+"F0.wireOp",EDGE,"E25.sketch_text.stroke-48"),sQuery(id+"F0.wireOp",EDGE,"E25.sketch_text.stroke-49"),sQuery(id+"F0.wireOp",EDGE,"E25.sketch_text.stroke-50"),sQuery(id+"F0.wireOp",EDGE,"E25.sketch_text.stroke-51"),sQuery(id+"F0.wireOp",EDGE,"E25.sketch_text.stroke-52"),sQuery(id+"F0.wireOp",EDGE,"E25.sketch_text.stroke-53"),sQuery(id+"F0.wireOp",EDGE,"E25.sketch_text.stroke-54"),sQuery(id+"F0.wireOp",EDGE,"E25.sketch_text.stroke-55"),sQuery(id+"F0.wireOp",EDGE,"E25.sketch_text.stroke-56"),sQuery(id+"F0.wireOp",EDGE,"E25.sketch_text.stroke-57"),sQuery(id+"F0.wireOp",EDGE,"E25.sketch_text.stroke-58"),sQuery(id+"F0.wireOp",EDGE,"E25.sketch_text.stroke-59"),sQuery(id+"F0.wireOp",EDGE,"E25.sketch_text.stroke-60"),sQuery(id+"F0.wireOp",EDGE,"E25.sketch_text.stroke-61"),sQuery(id+"F0.wireOp",EDGE,"E25.sketch_text.stroke-62"),sQuery(id+"F0.wireOp",EDGE,"E25.sketch_text.stroke-63"),sQuery(id+"F0.wireOp",EDGE,"E25.sketch_text.stroke-64"),sQuery(id+"F0.wireOp",EDGE,"E25.sketch_text.stroke-65"),sQuery(id+"F0.wireOp",EDGE,"E25.sketch_text.stroke-66"),sQuery(id+"F0.wireOp",EDGE,"E25.sketch_text.stroke-67"),sQuery(id+"F0.wireOp",EDGE,"E25.sketch_text.stroke-68"),sQuery(id+"F0.wireOp",EDGE,"E25.sketch_text.stroke-69"),sQuery(id+"F0.wireOp",EDGE,"E25.sketch_text.stroke-70"),sQuery(id+"F0.wireOp",EDGE,"E25.sketch_text.stroke-71"),sQuery(id+"F0.wireOp",EDGE,"E25.sketch_text.stroke-72"),sQuery(id+"F0.wireOp",EDGE,"E25.sketch_text.stroke-73"),sQuery(id+"F0.wireOp",EDGE,"E25.sketch_text.stroke-74"),sQuery(id+"F0.wireOp",EDGE,"E25.sketch_text.stroke-75"),sQuery(id+"F0.wireOp",EDGE,"E25.sketch_text.stroke-76"),sQuery(id+"F0.wireOp",EDGE,"E25.sketch_text.stroke-77"),sQuery(id+"F0.wireOp",EDGE,"E25.sketch_text.stroke-78"),sQuery(id+"F0.wireOp",EDGE,"E25.sketch_text.stroke-79"),sQuery(id+"F0.wireOp",EDGE,"E25.sketch_text.stroke-80"),sQuery(id+"F0.wireOp",EDGE,"E25.sketch_text.stroke-81"),sQuery(id+"F0.wireOp",EDGE,"E25.sketch_text.stroke-82"),sQuery(id+"F0.wireOp",EDGE,"E25.sketch_text.stroke-83"),sQuery(id+"F0.wireOp",EDGE,"E25.sketch_text.stroke-84"),sQuery(id+"F0.wireOp",EDGE,"E25.sketch_text.stroke-85"),sQuery(id+"F0.wireOp",EDGE,"E25.sketch_text.stroke-86"),sQuery(id+"F0.wireOp",EDGE,"E25.sketch_text.stroke-87"),sQuery(id+"F0.wireOp",EDGE,"E25.sketch_text.stroke-88"),sQuery(id+"F0.wireOp",EDGE,"E25.sketch_text.stroke-89"),sQuery(id+"F0.wireOp",EDGE,"E25.sketch_text.stroke-90"),sQuery(id+"F0.wireOp",EDGE,"E25.sketch_text.stroke-91"),sQuery(id+"F0.wireOp",EDGE,"E25.sketch_text.stroke-92"),sQuery(id+"F0.wireOp",EDGE,"E25.sketch_text.stroke-93"),sQuery(id+"F0.wireOp",EDGE,"E25.sketch_text.stroke-94"),sQuery(id+"F0.wireOp",EDGE,"E25.sketch_text.stroke-95"),sQuery(id+"F0.wireOp",EDGE,"E25.sketch_text.stroke-96"),sQuery(id+"F0.wireOp",EDGE,"E25.sketch_text.stroke-97"),sQuery(id+"F0.wireOp",EDGE,"E25.sketch_text.stroke-98"),sQuery(id+"F0.wireOp",EDGE,"E25.sketch_text.stroke-99"),sQuery(id+"F0.wireOp",EDGE,"E25.sketch_text.stroke-100"),sQuery(id+"F0.wireOp",EDGE,"E25.sketch_text.stroke-101"),sQuery(id+"F0.wireOp",EDGE,"E25.sketch_text.stroke-102"),sQuery(id+"F0.wireOp",EDGE,"E25.sketch_text.stroke-103"),sQuery(id+"F0.wireOp",EDGE,"E25.sketch_text.stroke-104"),sQuery(id+"F0.wireOp",EDGE,"E25.sketch_text.stroke-105"),sQuery(id+"F0.wireOp",EDGE,"E25.sketch_text.stroke-106"),sQuery(id+"F0.wireOp",EDGE,"E25.sketch_text.stroke-107"),sQuery(id+"F0.wireOp",EDGE,"E25.sketch_text.stroke-108"),sQuery(id+"F0.wireOp",EDGE,"E25.sketch_text.stroke-109"),sQuery(id+"F0.wireOp",EDGE,"E25.sketch_text.stroke-110"),sQuery(id+"F0.wireOp",EDGE,"E25.sketch_text.stroke-111"),sQuery(id+"F0.wireOp",EDGE,"E25.sketch_text.stroke-112"),sQuery(id+"F0.wireOp",EDGE,"E25.sketch_text.stroke-113"),sQuery(id+"F0.wireOp",EDGE,"E25.sketch_text.stroke-114"),sQuery(id+"F0.wireOp",EDGE,"E25.sketch_text.stroke-115"),sQuery(id+"F0.wireOp",EDGE,"E25.sketch_text.stroke-116"),sQuery(id+"F0.wireOp",EDGE,"E25.sketch_text.stroke-117"),sQuery(id+"F0.wireOp",EDGE,"E25.sketch_text.stroke-118"),sQuery(id+"F0.wireOp",EDGE,"E25.sketch_text.stroke-119"),sQuery(id+"F0.wireOp",EDGE,"E25.sketch_text.stroke-120"),sQuery(id+"F0.wireOp",EDGE,"E25.sketch_text.stroke-121"),sQuery(id+"F0.wireOp",EDGE,"E25.sketch_text.stroke-122"),sQuery(id+"F0.wireOp",EDGE,"E25.sketch_text.stroke-123"),sQuery(id+"F0.wireOp",EDGE,"E25.sketch_text.stroke-124"),sQuery(id+"F0.wireOp",EDGE,"E25.sketch_text.stroke-125"),sQuery(id+"F0.wireOp",EDGE,"E25.sketch_text.stroke-126"),sQuery(id+"F0.wireOp",EDGE,"E25.sketch_text.stroke-127"),sQuery(id+"F0.wireOp",EDGE,"E25.sketch_text.stroke-128"),sQuery(id+"F0.wireOp",EDGE,"E25.sketch_text.stroke-129"),sQuery(id+"F0.wireOp",EDGE,"E25.sketch_text.stroke-130"),sQuery(id+"F0.wireOp",EDGE,"E25.sketch_text.stroke-131"),sQuery(id+"F0.wireOp",EDGE,"E25.sketch_text.stroke-132"),sQuery(id+"F0.wireOp",EDGE,"E25.sketch_text.stroke-133"),sQuery(id+"F0.wireOp",EDGE,"E25.sketch_text.stroke-134"),sQuery(id+"F0.wireOp",EDGE,"E25.sketch_text.stroke-135"),sQuery(id+"F0.wireOp",EDGE,"E25.sketch_text.stroke-136"),sQuery(id+"F0.wireOp",EDGE,"E25.sketch_text.stroke-137"),sQuery(id+"F0.wireOp",EDGE,"E25.sketch_text.stroke-138"),sQuery(id+"F0.wireOp",EDGE,"E25.sketch_text.stroke-139"),sQuery(id+"F0.wireOp",EDGE,"E25.sketch_text.stroke-140"),sQuery(id+"F0.wireOp",EDGE,"E25.sketch_text.stroke-141"),sQuery(id+"F0.wireOp",EDGE,"E25.sketch_text.stroke-142"),sQuery(id+"F0.wireOp",EDGE,"E25.sketch_text.stroke-143"),sQuery(id+"F0.wireOp",EDGE,"E25.sketch_text.stroke-144"),sQuery(id+"F0.wireOp",EDGE,"E25.sketch_text.stroke-145"),sQuery(id+"F0.wireOp",EDGE,"E25.sketch_text.stroke-146"),sQuery(id+"F0.wireOp",EDGE,"E25.sketch_text.stroke-147"),sQuery(id+"F0.wireOp",EDGE,"E25.sketch_text.stroke-148"),sQuery(id+"F0.wireOp",EDGE,"E25.sketch_text.stroke-149"),sQuery(id+"F0.wireOp",EDGE,"E25.sketch_text.stroke-150"),sQuery(id+"F0.wireOp",EDGE,"E25.sketch_text.stroke-151"),sQuery(id+"F0.wireOp",EDGE,"E25.sketch_text.stroke-152"),sQuery(id+"F0.wireOp",EDGE,"E25.sketch_text.stroke-153"),sQuery(id+"F0.wireOp",EDGE,"E25.sketch_text.stroke-154"),sQuery(id+"F0.wireOp",EDGE,"E25.sketch_text.stroke-155"),sQuery(id+"F0.wireOp",EDGE,"E25.sketch_text.stroke-156"),sQuery(id+"F0.wireOp",EDGE,"E25.sketch_text.stroke-157"),sQuery(id+"F0.wireOp",EDGE,"E25.sketch_text.stroke-158"),sQuery(id+"F0.wireOp",EDGE,"E25.sketch_text.stroke-159"),sQuery(id+"F0.wireOp",EDGE,"E25.sketch_text.stroke-160"),sQuery(id+"F0.wireOp",EDGE,"E25.sketch_text.stroke-161"),sQuery(id+"F0.wireOp",EDGE,"E25.sketch_text.stroke-162"),sQuery(id+"F0.wireOp",EDGE,"E25.sketch_text.stroke-163"),sQuery(id+"F0.wireOp",EDGE,"E25.sketch_text.stroke-164"),sQuery(id+"F0.wireOp",EDGE,"E25.sketch_text.stroke-165"),sQuery(id+"F0.wireOp",EDGE,"E25.sketch_text.stroke-166"),sQuery(id+"F0.wireOp",EDGE,"E25.sketch_text.stroke-167"),sQuery(id+"F0.wireOp",EDGE,"E25.sketch_text.stroke-168"),sQuery(id+"F0.wireOp",EDGE,"E25.sketch_text.stroke-169"),sQuery(id+"F0.wireOp",EDGE,"E25.sketch_text.stroke-170"),sQuery(id+"F0.wireOp",EDGE,"E25.sketch_text.stroke-171"),sQuery(id+"F0.wireOp",EDGE,"E25.sketch_text.stroke-172"),sQuery(id+"F0.wireOp",EDGE,"E25.sketch_text.stroke-173"),sQuery(id+"F0.wireOp",EDGE,"E25.sketch_text.stroke-174"),sQuery(id+"F0.wireOp",EDGE,"E25.sketch_text.stroke-175"),sQuery(id+"F0.wireOp",EDGE,"E25.sketch_text.stroke-176"),sQuery(id+"F0.wireOp",EDGE,"E25.sketch_text.stroke-177"),sQuery(id+"F0.wireOp",EDGE,"E25.sketch_text.stroke-178"),sQuery(id+"F0.wireOp",EDGE,"E25.sketch_text.stroke-179"),sQuery(id+"F0.wireOp",EDGE,"E25.sketch_text.stroke-180"),sQuery(id+"F0.wireOp",EDGE,"E25.sketch_text.stroke-181"),sQuery(id+"F0.wireOp",EDGE,"E25.sketch_text.stroke-182"),sQuery(id+"F0.wireOp",EDGE,"E25.sketch_text.stroke-183"),sQuery(id+"F0.wireOp",EDGE,"E25.sketch_text.stroke-184"),sQuery(id+"F0.wireOp",EDGE,"E25.sketch_text.stroke-185"),sQuery(id+"F0.wireOp",EDGE,"E25.sketch_text.stroke-186"),sQuery(id+"F0.wireOp",EDGE,"E25.sketch_text.stroke-187"),sQuery(id+"F0.wireOp",EDGE,"E25.sketch_text.stroke-188"),sQuery(id+"F0.wireOp",EDGE,"E25.sketch_text.stroke-189"),sQuery(id+"F0.wireOp",EDGE,"E25.sketch_text.stroke-190"),sQuery(id+"F0.wireOp",EDGE,"E25.sketch_text.stroke-191"),sQuery(id+"F0.wireOp",EDGE,"E25.sketch_text.stroke-192"),sQuery(id+"F0.wireOp",EDGE,"E25.sketch_text.stroke-193"),sQuery(id+"F0.wireOp",EDGE,"E25.sketch_text.stroke-194"),sQuery(id+"F0.wireOp",EDGE,"E25.sketch_text.stroke-195"),sQuery(id+"F0.wireOp",EDGE,"E25.sketch_text.stroke-196"),sQuery(id+"F0.wireOp",EDGE,"E25.sketch_text.stroke-197"),sQuery(id+"F0.wireOp",EDGE,"E25.sketch_text.stroke-198"),sQuery(id+"F0.wireOp",EDGE,"E25.sketch_text.stroke-199"),sQuery(id+"F0.wireOp",EDGE,"E25.sketch_text.stroke-200"),sQuery(id+"F0.wireOp",EDGE,"E25.sketch_text.stroke-201"),sQuery(id+"F0.wireOp",EDGE,"E25.sketch_text.stroke-202"),sQuery(id+"F0.wireOp",EDGE,"E25.sketch_text.stroke-203"),sQuery(id+"F0.wireOp",EDGE,"E25.sketch_text.stroke-204"),sQuery(id+"F0.wireOp",EDGE,"E25.sketch_text.stroke-205"),sQuery(id+"F0.wireOp",EDGE,"E25.sketch_text.stroke-206"),sQuery(id+"F0.wireOp",EDGE,"E25.sketch_text.stroke-207"),sQuery(id+"F0.wireOp",EDGE,"E25.sketch_text.stroke-208"),sQuery(id+"F0.wireOp",EDGE,"E25.sketch_text.stroke-209"),sQuery(id+"F0.wireOp",EDGE,"E25.sketch_text.stroke-210"),sQuery(id+"F0.wireOp",EDGE,"E25.sketch_text.stroke-211"),sQuery(id+"F0.wireOp",EDGE,"E25.sketch_text.stroke-212"),sQuery(id+"F0.wireOp",EDGE,"E25.sketch_text.stroke-213"),sQuery(id+"F0.wireOp",EDGE,"E25.sketch_text.stroke-214"),sQuery(id+"F0.wireOp",EDGE,"E25.sketch_text.stroke-215"),sQuery(id+"F0.wireOp",EDGE,"E25.sketch_text.stroke-216"),sQuery(id+"F0.wireOp",EDGE,"E25.sketch_text.stroke-217"),sQuery(id+"F0.wireOp",EDGE,"E25.sketch_text.stroke-218"),sQuery(id+"F0.wireOp",EDGE,"E25.sketch_text.stroke-219"),sQuery(id+"F0.wireOp",EDGE,"E26"),sQuery(id+"F0.wireOp",EDGE,"E29.0"),sQuery(id+"F0.wireOp",EDGE,"E30.0"),sQuery(id+"F0.wireOp",EDGE,"E31"),sQuery(id+"F0.wireOp",EDGE,"E32"),sQuery(id+"F0.wireOp",EDGE,"E33"),sQuery(id+"F0.wireOp",EDGE,"E34"),sQuery(id+"F0.wireOp",EDGE,"E35"),sQuery(id+"F0.wireOp",EDGE,"E36"),sQuery(id+"F0.wireOp",EDGE,"E37.filletArc"),sQuery(id+"F0.wireOp",EDGE,"E38.filletArc"),sQuery(id+"F0.wireOp",EDGE,"E39.filletArc"),sQuery(id+"F0.wireOp",EDGE,"E40.filletArc"),sQuery(id+"F0.wireOp",EDGE,"E41"),sQuery(id+"F0.wireOp",EDGE,"E42"),sQuery(id+"F0.wireOp",EDGE,"E43"),sQuery(id+"F0.wireOp",EDGE,"E44"),sQuery(id+"F0.wireOp",EDGE,"E45"),sQuery(id+"F0.wireOp",EDGE,"E46"),sQuery(id+"F0.wireOp",EDGE,"E47"),sQuery(id+"F0.wireOp",EDGE,"E48"),sQuery(id+"F0.wireOp",EDGE,"E49"),sQuery(id+"F0.wireOp",EDGE,"E50"),sQuery(id+"F0.wireOp",EDGE,"E51"),sQuery(id+"F0.wireOp",EDGE,"E52"),sQuery(id+"F0.wireOp",EDGE,"E53"),sQuery(id+"F0.wireOp",EDGE,"E54"),sQuery(id+"F0.wireOp",EDGE,"E55.filletArc"),sQuery(id+"F0.wireOp",EDGE,"E56.filletArc"),sQuery(id+"F0.wireOp",EDGE,"E57.filletArc"),sQuery(id+"F0.wireOp",EDGE,"E58.filletArc"),sQuery(id+"F0.wireOp",EDGE,"E59.filletArc"),sQuery(id+"F0.wireOp",EDGE,"E60.filletArc"),sQuery(id+"F0.wireOp",EDGE,"E61.filletArc"),sQuery(id+"F0.wireOp",EDGE,"E62.filletArc"),sQuery(id+"F0.wireOp",EDGE,"E63.filletArc"),sQuery(id+"F0.wireOp",EDGE,"E64.filletArc"),sQuery(id+"F0.wireOp",EDGE,"E65.filletArc"),sQuery(id+"F0.wireOp",EDGE,"E66.filletArc"),sQuery(id+"F0.wireOp",EDGE,"E67"),sQuery(id+"F0.wireOp",EDGE,"E68"),sQuery(id+"F0.wireOp",EDGE,"E69"),sQuery(id+"F0.wireOp",EDGE,"E70"),sQuery(id+"F0.wireOp",EDGE,"E71"),sQuery(id+"F0.wireOp",EDGE,"E72"),sQuery(id+"F0.wireOp",EDGE,"E73"),sQuery(id+"F0.wireOp",EDGE,"E74"),sQuery(id+"F0.wireOp",EDGE,"E75"),sQuery(id+"F0.wireOp",EDGE,"E76.filletArc"),sQuery(id+"F0.wireOp",EDGE,"E77.filletArc"),sQuery(id+"F0.wireOp",EDGE,"E78.filletArc"),sQuery(id+"F0.wireOp",EDGE,"E79.filletArc"),sQuery(id+"F0.wireOp",EDGE,"E80.filletArc"),sQuery(id+"F0.wireOp",EDGE,"E81.filletArc"),sQuery(id+"F0.wireOp",EDGE,"E82.filletArc"),sQuery(id+"F0.wireOp",EDGE,"E83.filletArc"),sQuery(id+"F0.wireOp",EDGE,"E84.filletArc"),sQuery(id+"F0.wireOp",EDGE,"E86.MirrorCS"),sQuery(id+"F0.wireOp",EDGE,"E87.MirrorCS"),sQuery(id+"F0.wireOp",EDGE,"E88.MirrorCS"),sQuery(id+"F0.wireOp",EDGE,"E89.MirrorCS"),sQuery(id+"F0.wireOp",EDGE,"E90.MirrorCS"),sQuery(id+"F0.wireOp",EDGE,"E91.MirrorCS"),sQuery(id+"F0.wireOp",EDGE,"E92.MirrorCS"),sQuery(id+"F0.wireOp",EDGE,"E93.MirrorCS"),sQuery(id+"F0.wireOp",EDGE,"E94.MirrorCS"),sQuery(id+"F0.wireOp",EDGE,"E95.MirrorCS"),sQuery(id+"F0.wireOp",EDGE,"E96.MirrorCS"),sQuery(id+"F0.wireOp",EDGE,"E97.MirrorCS"),sQuery(id+"F0.wireOp",EDGE,"E98"),sQuery(id+"F0.wireOp",EDGE,"E99"),sQuery(id+"F0.wireOp",EDGE,"E100"),sQuery(id+"F0.wireOp",EDGE,"E101"),sQuery(id+"F0.wireOp",EDGE,"E102"),sQuery(id+"F0.wireOp",EDGE,"E103"),sQuery(id+"F0.wireOp",EDGE,"E104"),sQuery(id+"F0.wireOp",EDGE,"E105"),sQuery(id+"F0.wireOp",EDGE,"E106"),sQuery(id+"F0.wireOp",EDGE,"E107"),sQuery(id+"F0.wireOp",EDGE,"E108"),sQuery(id+"F0.wireOp",EDGE,"E109"),sQuery(id+"F0.wireOp",EDGE,"E110.MirrorCS"),sQuery(id+"F0.wireOp",EDGE,"E111"),sQuery(id+"F0.wireOp",EDGE,"E112"),sQuery(id+"F0.wireOp",EDGE,"E113"),sQuery(id+"F0.wireOp",EDGE,"E114"),sQuery(id+"F0.wireOp",EDGE,"E115"),sQuery(id+"F0.wireOp",EDGE,"E116"),sQuery(id+"F0.wireOp",EDGE,"E117"),sQuery(id+"F0.wireOp",EDGE,"E118"),sQuery(id+"F0.wireOp",EDGE,"E119"),sQuery(id+"F0.wireOp",EDGE,"E120"),sQuery(id+"F0.wireOp",EDGE,"E121"),sQuery(id+"F0.wireOp",EDGE,"E122"),sQuery(id+"F0.wireOp",EDGE,"E123.filletArc"),sQuery(id+"F0.wireOp",EDGE,"E124.filletArc"),sQuery(id+"F0.wireOp",EDGE,"E125.filletArc"),sQuery(id+"F0.wireOp",EDGE,"E126.filletArc"),sQuery(id+"F0.wireOp",EDGE,"E127.filletArc"),sQuery(id+"F0.wireOp",EDGE,"E128.filletArc"),sQuery(id+"F0.wireOp",EDGE,"E129.filletArc"),sQuery(id+"F0.wireOp",EDGE,"E130.filletArc"),sQuery(id+"F0.wireOp",EDGE,"E131.filletArc"),sQuery(id+"F0.wireOp",EDGE,"E132.filletArc"),sQuery(id+"F0.wireOp",EDGE,"E133.filletArc"),sQuery(id+"F0.wireOp",EDGE,"E134.filletArc"),sQuery(id+"F0.wireOp",EDGE,"E135.filletArc"),sQuery(id+"F0.wireOp",EDGE,"E136.filletArc"),sQuery(id+"F0.wireOp",EDGE,"E137.filletArc"),sQuery(id+"F0.wireOp",EDGE,"E138.filletArc"),sQuery(id+"F0.wireOp",EDGE,"E139.filletArc"),sQuery(id+"F0.wireOp",EDGE,"E140.filletArc"),sQuery(id+"F0.wireOp",EDGE,"E141.filletArc"),sQuery(id+"F0.wireOp",EDGE,"E142.filletArc"),sQuery(id+"F0.wireOp",EDGE,"E143.filletArc"),sQuery(id+"F0.wireOp",EDGE,"E144.filletArc"),sQuery(id+"F0.wireOp",EDGE,"E145.filletArc"),sQuery(id+"F0.wireOp",EDGE,"E146.filletArc"),sQuery(id+"F0.wireOp",EDGE,"E147.0.1.0"),sQuery(id+"F0.wireOp",EDGE,"E147.0.1.1"),sQuery(id+"F0.wireOp",EDGE,"E147.0.1.3"),sQuery(id+"F0.wireOp",EDGE,"E147.0.1.4"),sQuery(id+"F0.wireOp",EDGE,"E147.0.1.5"),sQuery(id+"F0.wireOp",EDGE,"E147.0.1.6"),sQuery(id+"F0.wireOp",EDGE,"E147.0.1.7"),sQuery(id+"F0.wireOp",EDGE,"E147.0.1.12"),sQuery(id+"F0.wireOp",EDGE,"E147.0.1.13"),sQuery(id+"F0.wireOp",EDGE,"E147.0.1.16"),sQuery(id+"F0.wireOp",EDGE,"E147.0.1.19"),sQuery(id+"F0.wireOp",EDGE,"E147.0.1.20"),sQuery(id+"F0.wireOp",EDGE,"E147.0.1.21"),sQuery(id+"F0.wireOp",EDGE,"E147.0.1.23"),sQuery(id+"F0.wireOp",EDGE,"E147.0.1.25"),sQuery(id+"F0.wireOp",EDGE,"E147.0.1.27"),sQuery(id+"F0.wireOp",EDGE,"E147.0.1.28"),sQuery(id+"F0.wireOp",EDGE,"E147.0.1.31"),sQuery(id+"F0.wireOp",EDGE,"E147.0.1.33"),sQuery(id+"F0.wireOp",EDGE,"E147.0.1.34"),sQuery(id+"F0.wireOp",EDGE,"E147.0.1.35"),sQuery(id+"F0.wireOp",EDGE,"E147.0.1.37"),sQuery(id+"F0.wireOp",EDGE,"E147.0.1.40"),sQuery(id+"F0.wireOp",EDGE,"E147.0.1.43"),sQuery(id+"F0.wireOp",EDGE,"E147.0.1.45"),sQuery(id+"F0.wireOp",EDGE,"E147.0.1.48"),sQuery(id+"F0.wireOp",EDGE,"E147.0.1.49"),sQuery(id+"F0.wireOp",EDGE,"E147.0.1.51"),sQuery(id+"F0.wireOp",EDGE,"E147.0.1.52"),sQuery(id+"F0.wireOp",EDGE,"E147.0.1.53"),sQuery(id+"F0.wireOp",EDGE,"E147.0.1.54"),sQuery(id+"F0.wireOp",EDGE,"E147.0.1.55"),sQuery(id+"F0.wireOp",EDGE,"E147.0.1.56"),sQuery(id+"F0.wireOp",EDGE,"E147.0.1.57"),sQuery(id+"F0.wireOp",EDGE,"E147.0.1.59"),sQuery(id+"F0.wireOp",EDGE,"E147.0.1.60"),sQuery(id+"F0.wireOp",EDGE,"E147.0.1.61"),sQuery(id+"F0.wireOp",EDGE,"E147.0.1.62"),sQuery(id+"F0.wireOp",EDGE,"E147.0.1.63"),sQuery(id+"F0.wireOp",EDGE,"E147.0.1.64"),sQuery(id+"F0.wireOp",EDGE,"E147.0.1.65"),sQuery(id+"F0.wireOp",EDGE,"E147.0.1.66"),sQuery(id+"F0.wireOp",EDGE,"E147.0.1.67"),sQuery(id+"F0.wireOp",EDGE,"E147.0.1.68"),sQuery(id+"F0.wireOp",EDGE,"E147.0.1.69"),sQuery(id+"F0.wireOp",EDGE,"E147.0.1.70"),sQuery(id+"F0.wireOp",EDGE,"E147.0.1.71"),sQuery(id+"F0.wireOp",EDGE,"E147.0.1.72"),sQuery(id+"F0.wireOp",EDGE,"E147.0.2.0"),sQuery(id+"F0.wireOp",EDGE,"E147.0.2.1"),sQuery(id+"F0.wireOp",EDGE,"E147.0.2.3"),sQuery(id+"F0.wireOp",EDGE,"E147.0.2.4"),sQuery(id+"F0.wireOp",EDGE,"E147.0.2.5"),sQuery(id+"F0.wireOp",EDGE,"E147.0.2.6"),sQuery(id+"F0.wireOp",EDGE,"E147.0.2.7"),sQuery(id+"F0.wireOp",EDGE,"E147.0.2.12"),sQuery(id+"F0.wireOp",EDGE,"E147.0.2.13"),sQuery(id+"F0.wireOp",EDGE,"E147.0.2.16"),sQuery(id+"F0.wireOp",EDGE,"E147.0.2.19"),sQuery(id+"F0.wireOp",EDGE,"E147.0.2.20"),sQuery(id+"F0.wireOp",EDGE,"E147.0.2.21"),sQuery(id+"F0.wireOp",EDGE,"E147.0.2.23"),sQuery(id+"F0.wireOp",EDGE,"E147.0.2.25"),sQuery(id+"F0.wireOp",EDGE,"E147.0.2.27"),sQuery(id+"F0.wireOp",EDGE,"E147.0.2.28"),sQuery(id+"F0.wireOp",EDGE,"E147.0.2.31"),sQuery(id+"F0.wireOp",EDGE,"E147.0.2.33"),sQuery(id+"F0.wireOp",EDGE,"E147.0.2.34"),sQuery(id+"F0.wireOp",EDGE,"E147.0.2.35"),sQuery(id+"F0.wireOp",EDGE,"E147.0.2.37"),sQuery(id+"F0.wireOp",EDGE,"E147.0.2.40"),sQuery(id+"F0.wireOp",EDGE,"E147.0.2.43"),sQuery(id+"F0.wireOp",EDGE,"E147.0.2.45"),sQuery(id+"F0.wireOp",EDGE,"E147.0.2.48"),sQuery(id+"F0.wireOp",EDGE,"E147.0.2.49"),sQuery(id+"F0.wireOp",EDGE,"E147.0.2.51"),sQuery(id+"F0.wireOp",EDGE,"E147.0.2.52"),sQuery(id+"F0.wireOp",EDGE,"E147.0.2.53"),sQuery(id+"F0.wireOp",EDGE,"E147.0.2.54"),sQuery(id+"F0.wireOp",EDGE,"E147.0.2.55"),sQuery(id+"F0.wireOp",EDGE,"E147.0.2.56"),sQuery(id+"F0.wireOp",EDGE,"E147.0.2.57"),sQuery(id+"F0.wireOp",EDGE,"E147.0.2.59"),sQuery(id+"F0.wireOp",EDGE,"E147.0.2.60"),sQuery(id+"F0.wireOp",EDGE,"E147.0.2.61"),sQuery(id+"F0.wireOp",EDGE,"E147.0.2.62"),sQuery(id+"F0.wireOp",EDGE,"E147.0.2.63"),sQuery(id+"F0.wireOp",EDGE,"E147.0.2.64"),sQuery(id+"F0.wireOp",EDGE,"E147.0.2.65"),sQuery(id+"F0.wireOp",EDGE,"E147.0.2.66"),sQuery(id+"F0.wireOp",EDGE,"E147.0.2.67"),sQuery(id+"F0.wireOp",EDGE,"E147.0.2.68"),sQuery(id+"F0.wireOp",EDGE,"E147.0.2.69"),sQuery(id+"F0.wireOp",EDGE,"E147.0.2.70"),sQuery(id+"F0.wireOp",EDGE,"E147.0.2.71"),sQuery(id+"F0.wireOp",EDGE,"E147.0.2.72")])],"isStart":true});
            var sketch = newSketch(context, id + "F2", { "sketchPlane" : qUnion([Q0])});
            skCircle(sketch, "E148", {"center": v(19.05, 146.05) * mm, "radius": 1.59 * mm});
            skCircle(sketch, "E149", {"center": v(19.05, 133.35) * mm, "radius": 1.59 * mm});
            skCircle(sketch, "E150", {"center": v(19.05, 222.25) * mm, "radius": 1.59 * mm});
            skCircle(sketch, "E151", {"center": v(19.05, 203.2) * mm, "radius": 1.59 * mm});
            skLineSegment(sketch, "E152", {"start": v(17.46, 203.2) * mm, "end": v(17.46, 222.25) * mm});
            skLineSegment(sketch, "E153", {"start": v(20.64, 203.2) * mm, "end": v(20.64, 222.25) * mm});
            skLineSegment(sketch, "E154", {"start": v(69.85, 123.67) * mm, "end": v(69.85, 211.74) * mm, "construction": true});
            skLineSegment(sketch, "E155.MirrorCS", {"start": v(119.06, 203.2) * mm, "end": v(119.06, 222.25) * mm});
            skLineSegment(sketch, "E156.MirrorCS", {"start": v(122.24, 203.2) * mm, "end": v(122.24, 222.25) * mm});
            skCircle(sketch, "E157.MirrorC", {"center": v(120.65, 222.25) * mm, "radius": 1.59 * mm});
            skCircle(sketch, "E158.MirrorC", {"center": v(120.65, 133.35) * mm, "radius": 1.59 * mm});
            skCircle(sketch, "E159.MirrorC", {"center": v(120.65, 146.05) * mm, "radius": 1.59 * mm});
            skCircle(sketch, "E160.MirrorC", {"center": v(120.65, 203.2) * mm, "radius": 1.59 * mm});
            skSolve(sketch);
        }
        {
            var Q0;
            Q0 = qSketchRegion(id + "F2", true);
            extrude(context, id + "F3", {"entities" : qUnion([Q0]), "operationType" : NewBodyOperationType.REMOVE, "oppositeDirection" : true, "depth" : 25.4 * mm});
        }
    });
